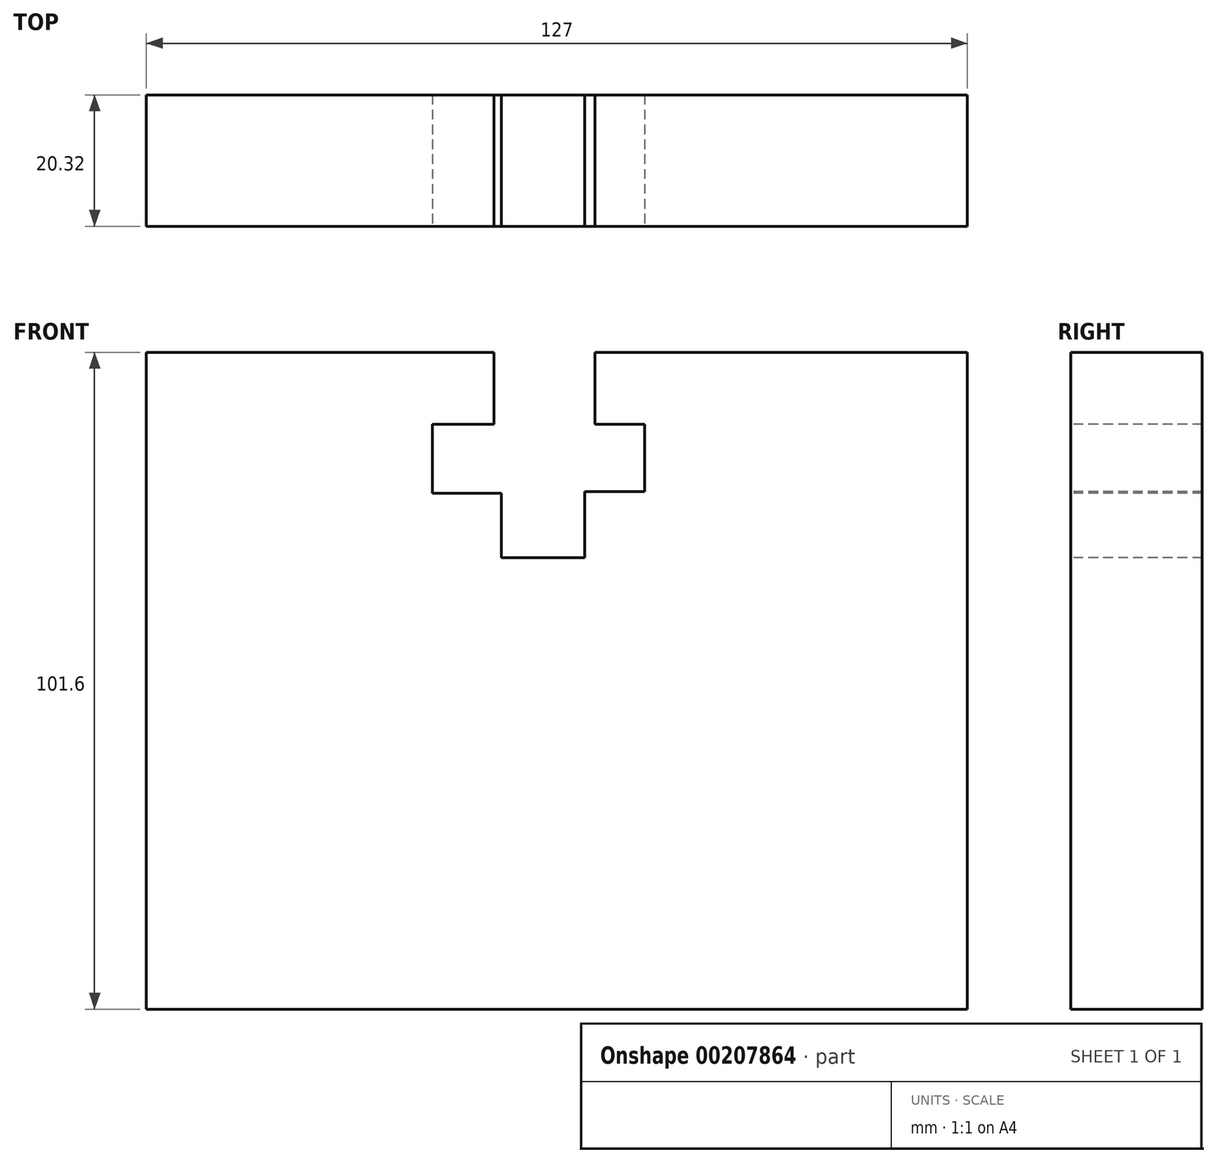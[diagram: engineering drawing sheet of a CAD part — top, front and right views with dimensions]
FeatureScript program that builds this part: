
annotation { "Feature Type Name" : "Feature", "Feature Type Description" : "" }
export const myFeature = defineFeature(function(context is Context, id is Id, definition is map)
    precondition{}
    {
        {
            var Q0;
            Q0=qCreatedBy(makeId("Front.planeOp"),FACE);
            var sketch = newSketch(context, id + "F0", { "sketchPlane" : qUnion([Q0])});
            skLineSegment(sketch, "E0.bottom", {"start": v(63.5, 50.8) * mm, "end": v(-63.5, 50.8) * mm});
            skLineSegment(sketch, "E0.top", {"start": v(63.5, -50.8) * mm, "end": v(-63.5, -50.8) * mm});
            skLineSegment(sketch, "E0.left", {"start": v(63.5, 50.8) * mm, "end": v(63.5, -50.8) * mm});
            skLineSegment(sketch, "E0.right", {"start": v(-63.5, 50.8) * mm, "end": v(-63.5, -50.8) * mm});
            skPoint(sketch, "E0.middle", {"position": v(0, 0) * mm});
            skSolve(sketch);
        }
        {
            var Q0;
            Q0=makeQuery(id+"F0.imprint","IMPRINT",FACE,{"disambiguationData":[TD([[makeQuery(id+"F0.imprint","IMPRINT",EDGE,{"derivedFrom":sQuery(id+"F0.wireOp",EDGE,"E0.bottom")}),1.0]])]});
            extrude(context, id + "F1", {"entities" : qUnion([Q0]), "depth" : 20.32 * mm});
        }
        {
            var Q0;
            Q0=makeQuery(id+"F1.opExtrude","CAP_FACE",FACE,{"disambiguationData":[OSD([sQuery(id+"F0.wireOp",EDGE,"E0.bottom"),sQuery(id+"F0.wireOp",EDGE,"E0.top"),sQuery(id+"F0.wireOp",EDGE,"E0.left"),sQuery(id+"F0.wireOp",EDGE,"E0.right")])],"isStart":false});
            var sketch = newSketch(context, id + "F2", { "sketchPlane" : qUnion([Q0])});
            skLineSegment(sketch, "E1", {"start": v(-9.75, 50.8) * mm, "end": v(-9.75, 39.67) * mm});
            skLineSegment(sketch, "E2", {"start": v(-9.75, 39.67) * mm, "end": v(-19.27, 39.67) * mm});
            skLineSegment(sketch, "E3", {"start": v(-19.27, 39.67) * mm, "end": v(-19.27, 29.01) * mm});
            skLineSegment(sketch, "E4", {"start": v(-19.27, 29.01) * mm, "end": v(-8.61, 29.01) * mm});
            skLineSegment(sketch, "E5", {"start": v(-8.61, 29.01) * mm, "end": v(-8.61, 19.04) * mm});
            skLineSegment(sketch, "E6", {"start": v(-8.61, 19.04) * mm, "end": v(4.3, 19.04) * mm});
            skLineSegment(sketch, "E7", {"start": v(4.3, 19.04) * mm, "end": v(4.3, 29.24) * mm});
            skLineSegment(sketch, "E8", {"start": v(4.3, 29.24) * mm, "end": v(13.6, 29.24) * mm});
            skLineSegment(sketch, "E9", {"start": v(13.6, 29.24) * mm, "end": v(13.6, 39.67) * mm});
            skLineSegment(sketch, "E10", {"start": v(13.6, 39.67) * mm, "end": v(5.9, 39.67) * mm});
            skLineSegment(sketch, "E11", {"start": v(5.9, 39.67) * mm, "end": v(5.9, 50.8) * mm});
            skLineSegment(sketch, "E12", {"start": v(5.9, 50.8) * mm, "end": v(-9.75, 50.8) * mm});
            skSolve(sketch);
        }
        {
            var Q0;
            Q0 = qSketchRegion(id + "F2", true);
            extrude(context, id + "F3", {"entities" : qUnion([Q0]), "operationType" : NewBodyOperationType.REMOVE, "oppositeDirection" : true, "depth" : 25.4 * mm});
        }
    });
